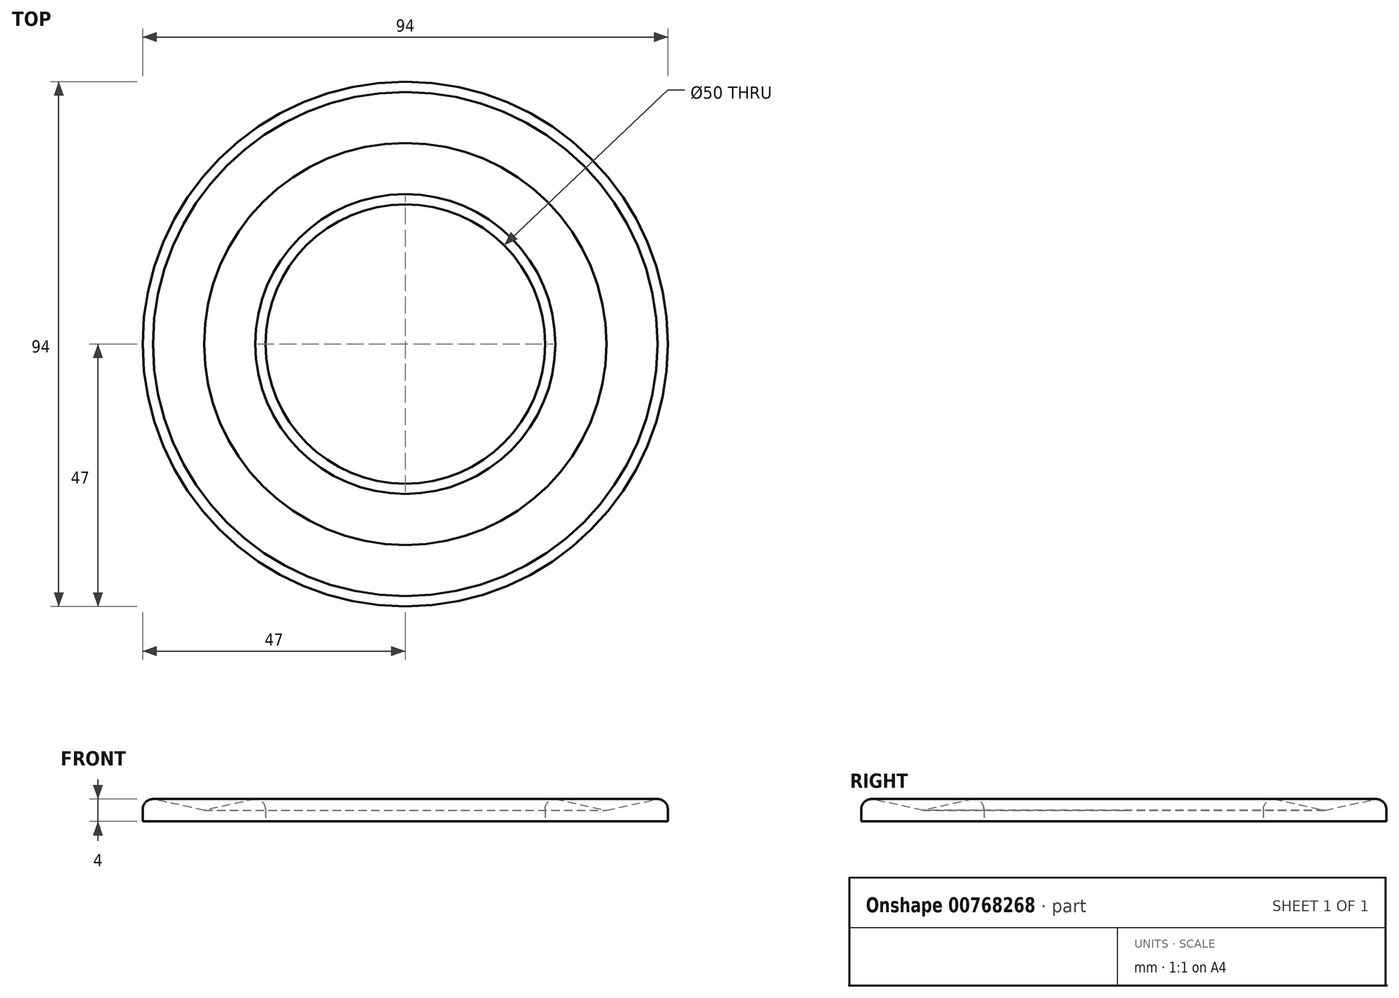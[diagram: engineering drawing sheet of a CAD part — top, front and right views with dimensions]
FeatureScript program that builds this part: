
annotation { "Feature Type Name" : "Feature", "Feature Type Description" : "" }
export const myFeature = defineFeature(function(context is Context, id is Id, definition is map)
    precondition{}
    {
        {
            var Q0;
            Q0=qCreatedBy(makeId("Front.planeOp"),FACE);
            var sketch = newSketch(context, id + "F0", { "sketchPlane" : qUnion([Q0])});
            skLineSegment(sketch, "E0", {"start": v(-25, 0) * mm, "end": v(-47, 0) * mm});
            skLineSegment(sketch, "E1", {"start": v(-47, 0) * mm, "end": v(-47, 2.15) * mm});
            skLineSegment(sketch, "E2", {"start": v(-25, 2.15) * mm, "end": v(-25, 0) * mm});
            skLineSegment(sketch, "E3", {"start": v(0, 0) * mm, "end": v(0, 4) * mm});
            skPoint(sketch, "E4.visualSharp", {"position": v(-47, 4) * mm});
            skArc(sketch, "E4.filletArc", {"start": v(-45.15, 4) * mm, "mid": v(-46.46, 3.46) * mm, "end": v(-47, 2.15) * mm});
            skPoint(sketch, "E5.visualSharp", {"position": v(-25, 4) * mm});
            skArc(sketch, "E5.filletArc", {"start": v(-25, 2.15) * mm, "mid": v(-25.54, 3.46) * mm, "end": v(-26.85, 4) * mm});
            skPoint(sketch, "E6.start.orphan", {"position": v(-35.08, 4) * mm});
            skLineSegment(sketch, "E7", {"start": v(-36, 2) * mm, "end": v(-45.15, 4) * mm});
            skLineSegment(sketch, "E8", {"start": v(-26.85, 4) * mm, "end": v(-36, 2) * mm});
            skPoint(sketch, "E9.start.orphan", {"position": v(-36, 4) * mm});
            skSolve(sketch);
        }
        {
            var Q0;
            Q0 = qSketchRegion(id + "F0", true);
            var Q1;
            Q1=sQuery(id+"F0.wireOp",EDGE,"E3");
            revolve(context, id + "F1", {"surfaceOperationType" : NewSurfaceOperationType.NEW, "entities" : qUnion([Q0]), "axis" : qUnion([Q1]), "revolveType" : RevolveType.FULL});
        }
    });
